# Revit family: Click Beam
name_source: partatom
category: Generic Models
revit_build: Autodesk Revit 2017 (Build: 20160225_1515(x64)
units: mm (PartAtom-declared; Revit-internal decimal feet)

## family parameters
Always vertical = Yes
Can host rebar = No
Cut with Voids When Loaded = No
Part Type = Normal
Room Calculation Point = No
Round Connector Dimension = Use Diameter
Shared = No
Work Plane-Based = No

## types (8) — shared parameters
Bottom Offset = 200 mm  [stored 0.656168 ft]
Finish = Pine, Scots
Height = 500 mm  [stored 1.64042 ft]
Model = Click Beam

## per-type parameters (varying)
| type | Length | Width |
| 40X120 | 120 mm  [stored 0.393701 ft] | 40 mm  [stored 0.131234 ft] |
| 60X80 | 80 mm  [stored 0.262467 ft] | 60 mm  [stored 0.19685 ft] |
| 40X150 | 150 mm | 40 mm  [stored 0.131234 ft] |
| 40X200 | 200 mm  [stored 0.656168 ft] | 40 mm  [stored 0.131234 ft] |
| 60X120 | 120 mm  [stored 0.393701 ft] | 60 mm  [stored 0.19685 ft] |
| 40X80 | 80 mm  [stored 0.262467 ft] | 40 mm  [stored 0.131234 ft] |
| 60X150 | 150 mm | 60 mm  [stored 0.19685 ft] |
| 60X200 | 200 mm  [stored 0.656168 ft] | 60 mm  [stored 0.19685 ft] |

note: [stored X ft] marks values corroborated as IEEE doubles in the binary element streams (Revit-internal decimal feet)

## geometry (parser evidence)
native form markers: Sweep x3
no freeform markers — native parametric forms only
